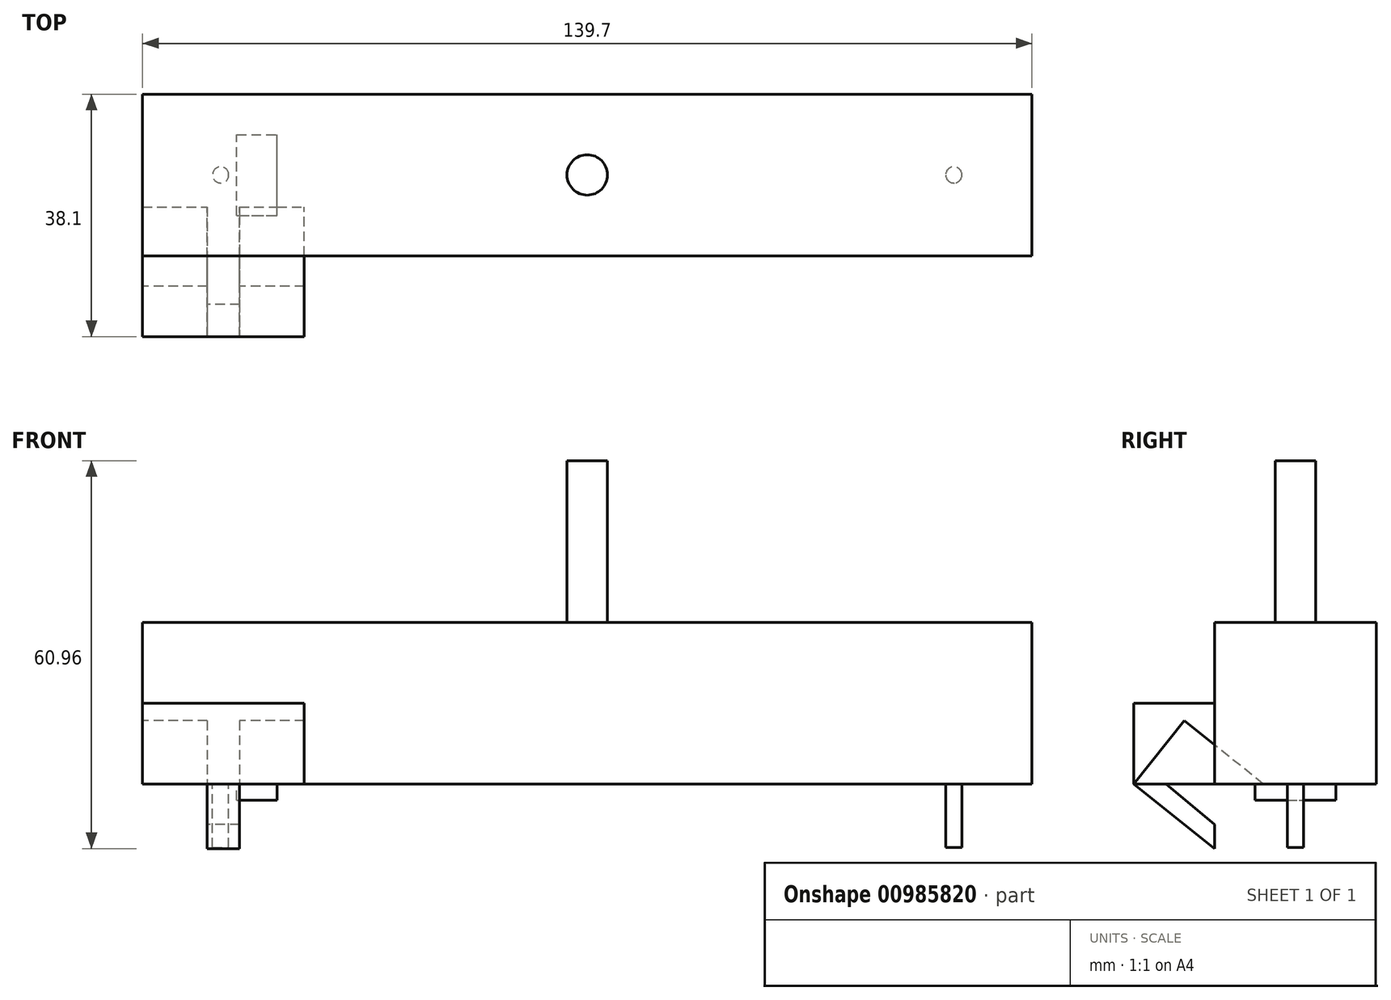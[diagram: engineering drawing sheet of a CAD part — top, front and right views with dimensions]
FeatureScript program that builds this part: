
annotation { "Feature Type Name" : "Feature", "Feature Type Description" : "" }
export const myFeature = defineFeature(function(context is Context, id is Id, definition is map)
    precondition{}
    {
        {
            var Q0;
            Q0=qCreatedBy(makeId("Top.planeOp"),FACE);
            var sketch = newSketch(context, id + "F0", { "sketchPlane" : qUnion([Q0])});
            skLineSegment(sketch, "E0.bottom", {"start": v(-69.85, 12.7) * mm, "end": v(69.85, 12.7) * mm});
            skLineSegment(sketch, "E0.top", {"start": v(-69.85, -12.7) * mm, "end": v(69.85, -12.7) * mm});
            skLineSegment(sketch, "E0.left", {"start": v(-69.85, 12.7) * mm, "end": v(-69.85, -12.7) * mm});
            skLineSegment(sketch, "E0.right", {"start": v(69.85, 12.7) * mm, "end": v(69.85, -12.7) * mm});
            skPoint(sketch, "E0.middle", {"position": v(0, 0) * mm});
            skSolve(sketch);
        }
        {
            var Q0;
            Q0 = qSketchRegion(id + "F0", true);
            extrude(context, id + "F1", {"entities" : qUnion([Q0]), "depth" : 25.4 * mm, "offsetDistance" : 25.4 * mm});
        }
        {
            var Q0;
            Q0=makeQuery(id+"F1.opExtrude","CAP_FACE",FACE,{"disambiguationData":[OSD([sQuery(id+"F0.wireOp",EDGE,"E0.bottom"),sQuery(id+"F0.wireOp",EDGE,"E0.top"),sQuery(id+"F0.wireOp",EDGE,"E0.left"),sQuery(id+"F0.wireOp",EDGE,"E0.right")])],"isStart":true});
            var sketch = newSketch(context, id + "F2", { "sketchPlane" : qUnion([Q0])});
            skCircle(sketch, "E1", {"center": v(-57.58, 0) * mm, "radius": 1.27 * mm});
            skCircle(sketch, "E2", {"center": v(57.58, 0) * mm, "radius": 1.27 * mm});
            skSolve(sketch);
        }
        {
            var Q0;
            Q0 = qSketchRegion(id + "F2", true);
            extrude(context, id + "F3", {"entities" : qUnion([Q0]), "operationType" : NewBodyOperationType.ADD, "depth" : 10 * mm, "offsetDistance" : 25.4 * mm});
        }
        {
            var Q0;
            Q0=makeQuery(id+"F1.opExtrude","SWEPT_FACE",FACE,{"disambiguationData":[OSD([sQuery(id+"F0.wireOp",EDGE,"E0.top")])]});
            var sketch = newSketch(context, id + "F4", { "sketchPlane" : qUnion([Q0])});
            skLineSegment(sketch, "E3.bottom", {"start": v(-69.85, 0) * mm, "end": v(-44.45, 0) * mm});
            skLineSegment(sketch, "E3.top", {"start": v(-69.85, 12.7) * mm, "end": v(-44.45, 12.7) * mm});
            skLineSegment(sketch, "E3.left", {"start": v(-69.85, 0) * mm, "end": v(-69.85, 12.7) * mm});
            skLineSegment(sketch, "E3.right", {"start": v(-44.45, 0) * mm, "end": v(-44.45, 12.7) * mm});
            skSolve(sketch);
        }
        {
            var Q0;
            Q0 = qSketchRegion(id + "F4", true);
            extrude(context, id + "F5", {"entities" : qUnion([Q0]), "operationType" : NewBodyOperationType.ADD, "depth" : 12.7 * mm, "offsetDistance" : 25.4 * mm});
        }
        {
            var Q0;
            Q0=makeQuery(id+"F5.boolean.opBoolean","MERGE",FACE,{"derivedFrom":[makeQuery(id+"F1.opExtrude","SWEPT_FACE",FACE,{"disambiguationData":[OSD([sQuery(id+"F0.wireOp",EDGE,"E0.left")])]}),makeQuery(id+"F5.opExtrude","SWEPT_FACE",FACE,{"disambiguationData":[OSD([sQuery(id+"F4.wireOp",EDGE,"E3.left")])]})]});
            var sketch = newSketch(context, id + "F6", { "sketchPlane" : qUnion([Q0])});
            skLineSegment(sketch, "E4.bottom", {"start": v(12.7, 0) * mm, "end": v(25.4, 0) * mm});
            skLineSegment(sketch, "E4.top", {"start": v(12.7, -10.16) * mm, "end": v(25.4, -10.16) * mm});
            skLineSegment(sketch, "E4.left", {"start": v(12.7, 0) * mm, "end": v(12.7, -10.16) * mm});
            skLineSegment(sketch, "E4.right", {"start": v(25.4, 0) * mm, "end": v(25.4, -10.16) * mm});
            skLineSegment(sketch, "E5", {"start": v(20.32, 0) * mm, "end": v(12.7, -6.35) * mm});
            skLineSegment(sketch, "E6", {"start": v(12.7, -10.16) * mm, "end": v(25.4, 0) * mm});
            skSolve(sketch);
        }
        {
            var Q0;
            {var subQ2=sQuery(id+"F6.wireOp",EDGE,"E5");Q0=makeQuery(id+"F6.imprint","IMPRINT",FACE,{"disambiguationData":[TD([[makeQuery(id+"F6.imprint","IMPRINT",EDGE,{"derivedFrom":subQ2}),1.0]])]});}
            extrude(context, id + "F7", {"entities" : qUnion([Q0]), "oppositeDirection" : true, "depth" : 25.4 * mm, "offsetDistance" : 25.4 * mm});
        }
        {
            var Q0;
            Q0=makeQuery(id+"F7.opExtrude","SWEPT_FACE",FACE,{"disambiguationData":[OSD([sQuery(id+"F6.wireOp",EDGE,"E6")])]});
            var sketch = newSketch(context, id + "F8", { "sketchPlane" : qUnion([Q0])});
            skLineSegment(sketch, "E7.bottom", {"start": v(-69.85, 19.83) * mm, "end": v(-59.7, 19.83) * mm});
            skLineSegment(sketch, "E7.top", {"start": v(-69.85, 3.57) * mm, "end": v(-59.7, 3.57) * mm});
            skLineSegment(sketch, "E7.left", {"start": v(-69.85, 19.83) * mm, "end": v(-69.85, 3.57) * mm});
            skLineSegment(sketch, "E7.right", {"start": v(-59.7, 19.83) * mm, "end": v(-59.7, 3.57) * mm});
            skLineSegment(sketch, "E8.bottom", {"start": v(-44.45, 19.83) * mm, "end": v(-54.61, 19.83) * mm});
            skLineSegment(sketch, "E8.top", {"start": v(-44.45, 3.57) * mm, "end": v(-54.61, 3.57) * mm});
            skLineSegment(sketch, "E8.left", {"start": v(-44.45, 19.83) * mm, "end": v(-44.45, 3.57) * mm});
            skLineSegment(sketch, "E8.right", {"start": v(-54.61, 19.83) * mm, "end": v(-54.61, 3.57) * mm});
            skLineSegment(sketch, "E9", {"start": v(-59.7, 19.83) * mm, "end": v(-54.61, 19.83) * mm});
            skLineSegment(sketch, "E10", {"start": v(-59.7, 3.57) * mm, "end": v(-54.61, 3.57) * mm});
            skSolve(sketch);
        }
        {
            var Q0;
            Q0=makeQuery(id+"F8.imprint","IMPRINT",FACE,{"disambiguationData":[TD([[makeQuery(id+"F8.imprint","IMPRINT",EDGE,{"derivedFrom":sQuery(id+"F8.wireOp",EDGE,"E8.bottom")}),1.0]])]});
            var Q1;
            Q1=makeQuery(id+"F8.imprint","IMPRINT",FACE,{"disambiguationData":[TD([[makeQuery(id+"F8.imprint","IMPRINT",EDGE,{"derivedFrom":sQuery(id+"F8.wireOp",EDGE,"E7.bottom")}),1.0]])]});
            extrude(context, id + "F9", {"entities" : qUnion([Q0, Q1]), "operationType" : NewBodyOperationType.REMOVE, "oppositeDirection" : true, "depth" : 12.7 * mm, "offsetDistance" : 25.4 * mm});
        }
        {
            var Q0;
            Q0=makeQuery(id+"F5.boolean.opBoolean","MERGE",FACE,{"derivedFrom":[makeQuery(id+"F1.opExtrude","CAP_FACE",FACE,{"disambiguationData":[OSD([sQuery(id+"F0.wireOp",EDGE,"E0.bottom"),sQuery(id+"F0.wireOp",EDGE,"E0.top"),sQuery(id+"F0.wireOp",EDGE,"E0.left"),sQuery(id+"F0.wireOp",EDGE,"E0.right")])],"isStart":true}),makeQuery(id+"F5.opExtrude","SWEPT_FACE",FACE,{"disambiguationData":[OSD([sQuery(id+"F4.wireOp",EDGE,"E3.bottom")])]})]});
            var sketch = newSketch(context, id + "F10", { "sketchPlane" : qUnion([Q0])});
            skLineSegment(sketch, "E11.bottom", {"start": v(-55.04, 6.35) * mm, "end": v(-48.69, 6.35) * mm});
            skLineSegment(sketch, "E11.top", {"start": v(-55.04, -6.35) * mm, "end": v(-48.69, -6.35) * mm});
            skLineSegment(sketch, "E11.left", {"start": v(-55.04, 6.35) * mm, "end": v(-55.04, -6.35) * mm});
            skLineSegment(sketch, "E11.right", {"start": v(-48.69, 6.35) * mm, "end": v(-48.69, -6.35) * mm});
            skSolve(sketch);
        }
        {
            var Q0;
            Q0 = qSketchRegion(id + "F10", true);
            extrude(context, id + "F11", {"entities" : qUnion([Q0]), "operationType" : NewBodyOperationType.ADD, "depth" : 2.54 * mm, "offsetDistance" : 25.4 * mm});
        }
        {
            var Q0;
            Q0=makeQuery(id+"F1.opExtrude","CAP_FACE",FACE,{"disambiguationData":[OSD([sQuery(id+"F0.wireOp",EDGE,"E0.bottom"),sQuery(id+"F0.wireOp",EDGE,"E0.top"),sQuery(id+"F0.wireOp",EDGE,"E0.left"),sQuery(id+"F0.wireOp",EDGE,"E0.right")])],"isStart":false});
            var sketch = newSketch(context, id + "F12", { "sketchPlane" : qUnion([Q0])});
            skCircle(sketch, "E12", {"center": v(0, 0) * mm, "radius": 3.17 * mm});
            skSolve(sketch);
        }
        {
            var Q0;
            Q0 = qSketchRegion(id + "F12", true);
            extrude(context, id + "F13", {"entities" : qUnion([Q0]), "operationType" : NewBodyOperationType.ADD, "depth" : 25.4 * mm, "offsetDistance" : 25.4 * mm});
        }
    });
